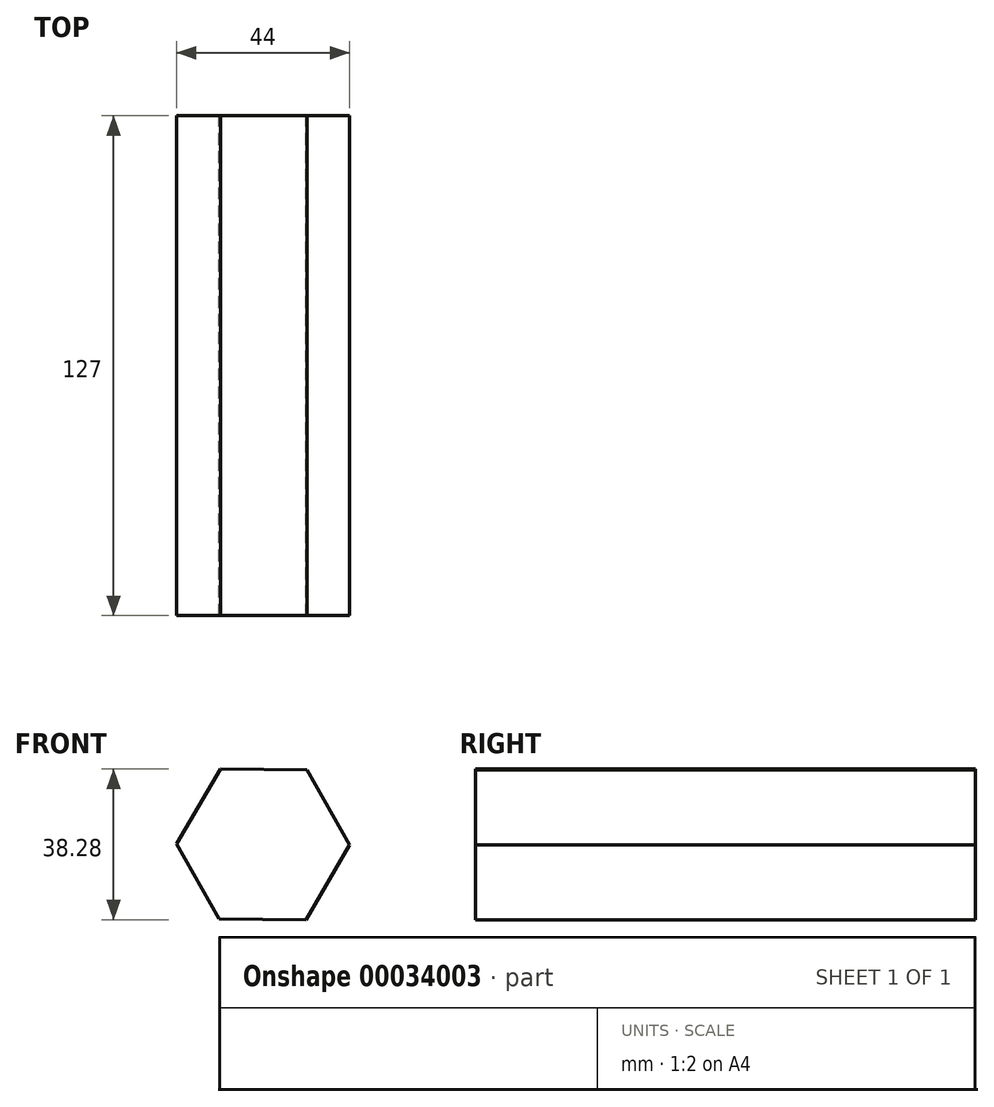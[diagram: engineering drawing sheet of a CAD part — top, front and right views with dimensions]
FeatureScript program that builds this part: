
annotation { "Feature Type Name" : "Feature", "Feature Type Description" : "" }
export const myFeature = defineFeature(function(context is Context, id is Id, definition is map)
    precondition{}
    {
        {
            var Q0;
            Q0=qCreatedBy(makeId("Front.planeOp"),FACE);
            var sketch = newSketch(context, id + "F0", { "sketchPlane" : qUnion([Q0])});
            skCircle(sketch, "E0.cCircle", {"center": v(0, 0) * mm, "radius": 19.05 * mm, "construction": true});
            skLineSegment(sketch, "E0.0", {"start": v(11.15, 18.96) * mm, "end": v(22, -0.17) * mm});
            skLineSegment(sketch, "E0.1", {"start": v(22, -0.17) * mm, "end": v(10.85, -19.14) * mm});
            skLineSegment(sketch, "E0.2", {"start": v(10.85, -19.14) * mm, "end": v(-11.15, -18.96) * mm});
            skLineSegment(sketch, "E0.3", {"start": v(-11.15, -18.96) * mm, "end": v(-22, 0.17) * mm});
            skLineSegment(sketch, "E0.4", {"start": v(-22, 0.17) * mm, "end": v(-10.85, 19.14) * mm});
            skLineSegment(sketch, "E0.5", {"start": v(-10.85, 19.14) * mm, "end": v(11.15, 18.96) * mm});
            skPoint(sketch, "E0.0.midPoint", {"position": v(16.57, 9.4) * mm});
            skSolve(sketch);
        }
        {
            var Q0;
            Q0 = qSketchRegion(id + "F0", true);
            extrude(context, id + "F1", {"entities" : qUnion([Q0]), "depth" : 127 * mm});
        }
    });
